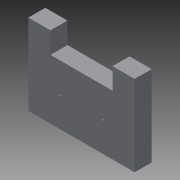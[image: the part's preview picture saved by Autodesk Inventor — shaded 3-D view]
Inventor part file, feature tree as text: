
AUTODESK INVENTOR PART (.ipt)
format: ipt  version: 2015 (Build 190159000, 159)  size: 82,432 bytes
history: native  units: mm
features: extrude x1, sketch x1
ambient origin geometry x8: Origin, YZ Plane, XZ Plane, XY Plane, X Axis, Y Axis, Z Axis, Center Point
bodies: Solid1 (feature_tree)
feature tree (2):
  extrude  "Extrusion1"  Depth=9.5mm
  sketch  "Sketch1"  dims[d0=12.5mm d1=9.5mm d2=2.6mm d7=0.2mm d9=0.2mm d10=2.0mm d11=0.0mm d17=2.6mm d18=2.5mm d19=7.3mm]
